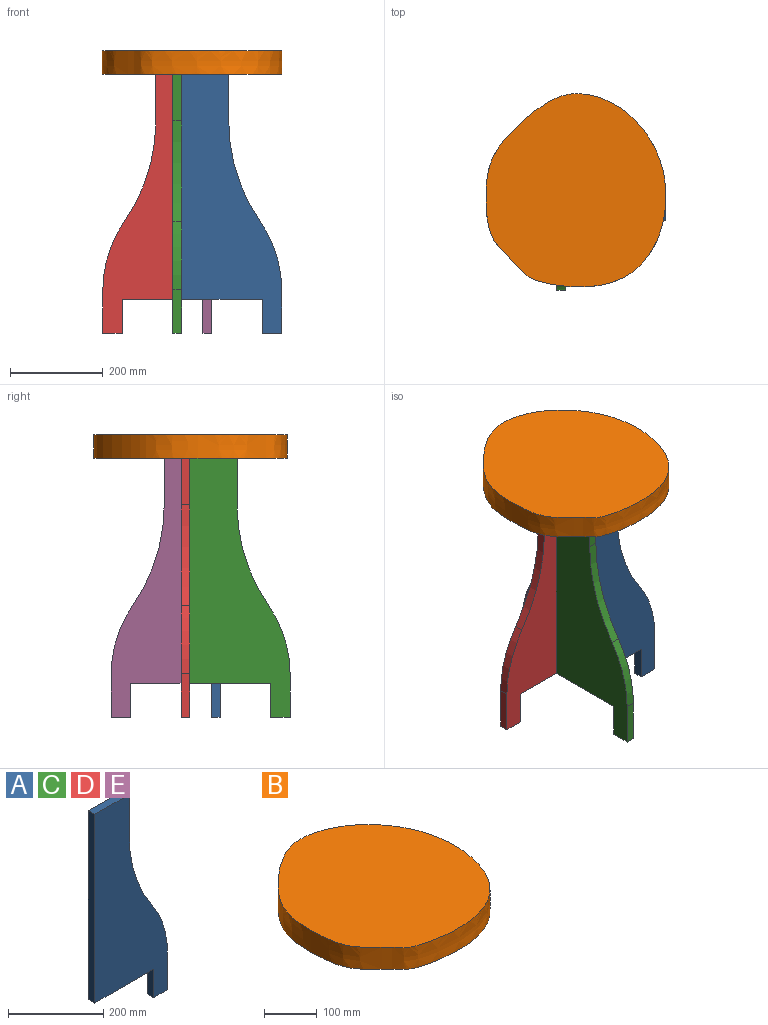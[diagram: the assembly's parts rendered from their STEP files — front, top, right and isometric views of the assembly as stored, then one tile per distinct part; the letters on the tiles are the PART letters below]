
ASSEMBLY  parts=5 mates=1
PART A: 11 faces, bbox 215.9x19.1x558.8 mm
  f0: plane 41.51x19.05mm, normal (0,0,-1), area 790.7mm2, adj f1,f2,f7,f10
  f1: plane 558.8x215.9mm, normal (0,-1,0), area 74059.7mm2, adj f0,f3,f4,f5,f6,f7,f8,f9
  f2: plane 558.8x215.9mm, normal (0,1,0), area 74059.7mm2, adj f0,f3,f4,f5,f6,f7,f8,f9
  f3: plane 485.36x19.05mm, normal (-1,0,0), area 9246mm2, adj f1,f2,f4,f9
  f4: plane 101.6x19.05mm, normal (0,0,1), area 1935.5mm2, adj f1,f2,f3,f5
  f5: plane 100.65x19.05mm, normal (1,0,0), area 1917.4mm2, adj f1,f2,f4,f6
  f6: cylinder r=380.83mm len=217.58mm, axis (0,-1,0), area 4411.8mm2, adj f1,f2,f5,f8
  f7: plane 93.89x19.05mm, normal (1,0,0), area 1788.7mm2, adj f0,f1,f2,f8
  f8: cylinder r=256.74mm len=146.68mm, axis (0,-1,0), area 2974.2mm2, adj f1,f2,f6,f7
  f9: plane 174.39x19.05mm, normal (0,0,-1), area 3322.1mm2, adj f1,f2,f3,f10
  f10: plane 73.45x19.05mm, normal (-1,0,0), area 1399.1mm2, adj f0,f1,f2,f9
PART B: 6 faces, bbox 393.3x420.7x50.8 mm
  f0: extruded ~416.72x387.36mm, area 63811.7mm2, adj f1,f2,f3
  f1: cylinder r=215.9mm len=50.8mm, axis (0,0,-1), area 505.3mm2, adj f0,f2,f3
  f2: plane 420.71x393.28mm, normal (0,0,1), area 127441.8mm2, adj f0,f1
  f3: plane 420.71x393.28mm, normal (0,0,-1), area 127196.3mm2, adj f0,f1,f4
  f4: cylinder r=8.84mm len=17.68mm, axis (0,0,-1), area 705.4mm2, adj f3,f5
  f5: plane 17.68x17.68mm, normal (0,0,-1), area 245.5mm2, adj f4
PART C: same geometry as A
PART D: same geometry as A
PART E: same geometry as A
PLACE A t=(-23.02,-37.34,-609.6)mm
PLACE B t=(0,-14.32,-50.8)mm
PLACE C rot(axis=(0,0,-1),90deg) t=(-23.03,8.7,-609.6)mm
PLACE D rot(axis=(0,0,-1),180deg) t=(23.02,8.71,-609.6)mm
PLACE E rot(axis=(0,0,1),90deg) t=(23.03,-37.33,-609.6)mm
MATE fastened B.f3 <-> A.f4  axis (0,0,-1) through (0.8,0.76,-50.8)mm
